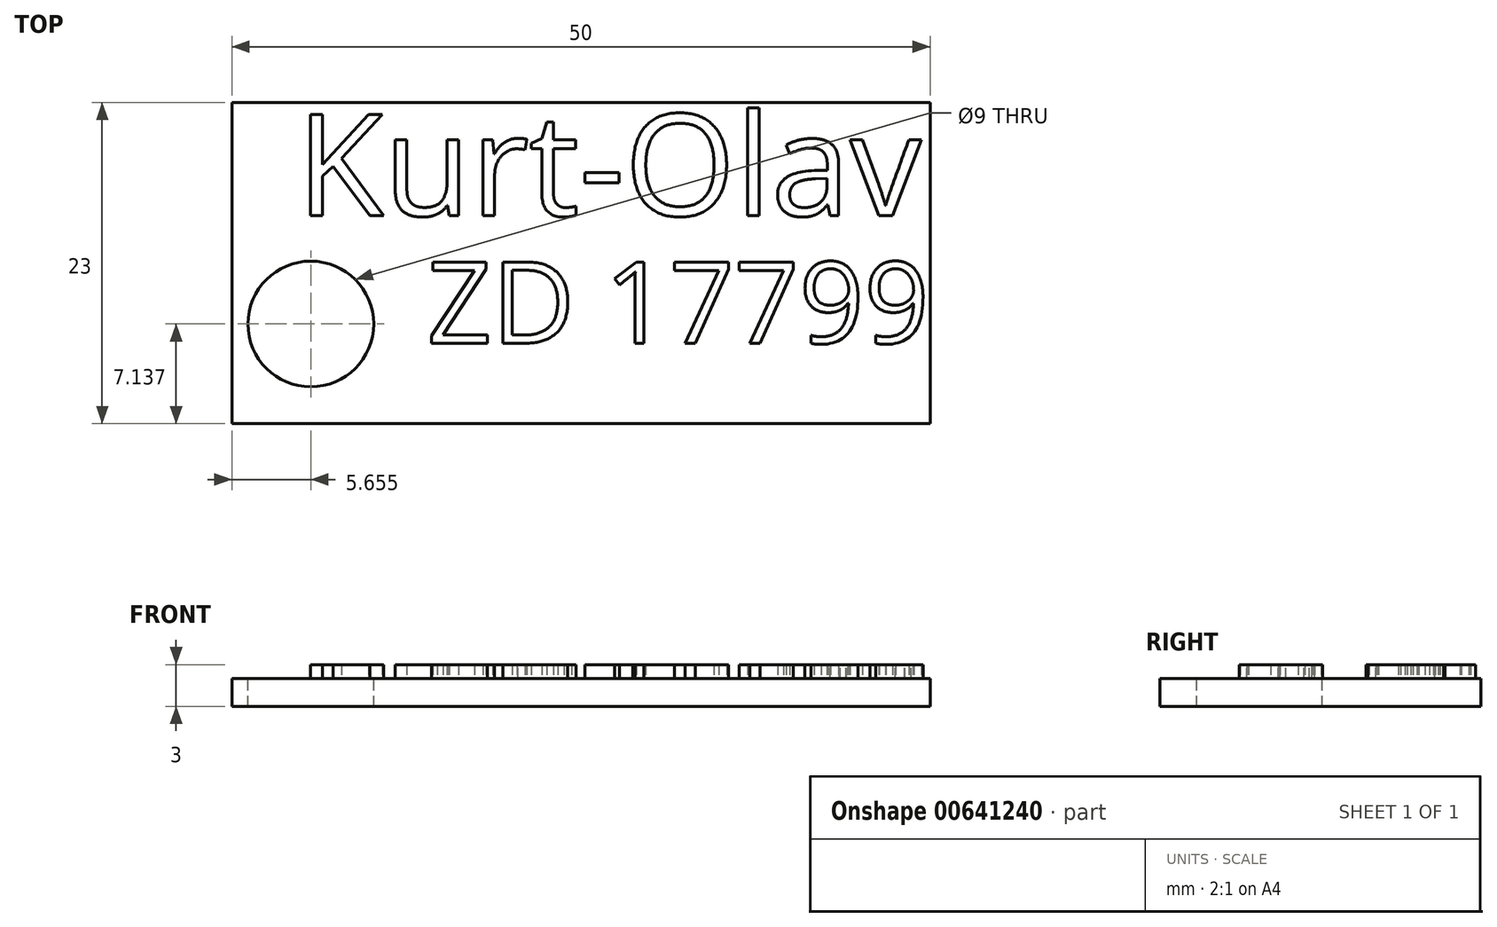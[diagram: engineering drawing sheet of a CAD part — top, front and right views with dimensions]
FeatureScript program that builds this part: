
annotation { "Feature Type Name" : "Feature", "Feature Type Description" : "" }
export const myFeature = defineFeature(function(context is Context, id is Id, definition is map)
    precondition{}
    {
        {
            var Q0;
            Q0=qCreatedBy(makeId("Top.planeOp"),FACE);
            var sketch = newSketch(context, id + "F0", { "sketchPlane" : qUnion([Q0])});
            skLineSegment(sketch, "E0.bottom", {"start": v(25, -11.5) * mm, "end": v(-25, -11.5) * mm});
            skLineSegment(sketch, "E0.top", {"start": v(25, 11.5) * mm, "end": v(-25, 11.5) * mm});
            skLineSegment(sketch, "E0.left", {"start": v(25, -11.5) * mm, "end": v(25, 11.5) * mm});
            skLineSegment(sketch, "E0.right", {"start": v(-25, -11.5) * mm, "end": v(-25, 11.5) * mm});
            skPoint(sketch, "E0.middle", {"position": v(0, 0) * mm});
            skSolve(sketch);
        }
        {
            var Q0;
            Q0=makeQuery(id+"F0.imprint","IMPRINT",FACE,{"disambiguationData":[TD([[makeQuery(id+"F0.imprint","IMPRINT",EDGE,{"derivedFrom":sQuery(id+"F0.wireOp",EDGE,"E0.bottom")}),-1.0]])]});
            extrude(context, id + "F1", {"entities" : qUnion([Q0]), "depth" : 2 * mm, "offsetDistance" : 25 * mm});
        }
        {
            var Q0;
            Q0=makeQuery(id+"F1.opExtrude","CAP_FACE",FACE,{"disambiguationData":[OSD([sQuery(id+"F0.wireOp",EDGE,"E0.bottom"),sQuery(id+"F0.wireOp",EDGE,"E0.top"),sQuery(id+"F0.wireOp",EDGE,"E0.left"),sQuery(id+"F0.wireOp",EDGE,"E0.right")])],"isStart":false});
            var sketch = newSketch(context, id + "F2", { "sketchPlane" : qUnion([Q0])});
            skText(sketch, "E1", { "text": "Kurt-Olav", "fontName": "OpenSans-Regular.ttf"});
            const initialGuessF2  = {"E1": [-0.02036, 0.00339, 1, 0, 0.00732]};
            skSetInitialGuess(sketch, initialGuessF2);
            skSolve(sketch);
        }
        {
            var Q0;
            Q0 = qSketchRegion(id + "F2", true);
            extrude(context, id + "F3", {"entities" : qUnion([Q0]), "operationType" : NewBodyOperationType.ADD, "depth" : 1 * mm, "offsetDistance" : 25 * mm});
        }
        {
            var Q0;
            {var subQ0=sQuery(id+"F0.wireOp",EDGE,"E0.top");var subQ1=sQuery(id+"F0.wireOp",EDGE,"E0.right");var subQ2=sQuery(id+"F0.wireOp",EDGE,"E0.bottom");var subQ3=sQuery(id+"F0.wireOp",EDGE,"E0.left");Q0=makeQuery(id+"F3.boolean.opBoolean","SPLIT",FACE,{"disambiguationData":[TD([makeQuery(id+"F1.opExtrude","SWEPT_FACE",FACE,{"disambiguationData":[OSD([subQ2])]})])],"derivedFrom":makeQuery(id+"F1.opExtrude","CAP_FACE",FACE,{"disambiguationData":[OSD([subQ2,subQ0,subQ3,subQ1])],"isStart":false})});}
            var sketch = newSketch(context, id + "F4", { "sketchPlane" : qUnion([Q0])});
            skText(sketch, "E2", { "text": "ZD 17799", "fontName": "OpenSans-Regular.ttf"});
            const initialGuessF4  = {"E2": [-0.01103, -0.00574, 1, 0, 0.00586]};
            skSetInitialGuess(sketch, initialGuessF4);
            skSolve(sketch);
        }
        {
            var Q0;
            Q0 = qSketchRegion(id + "F4", true);
            extrude(context, id + "F5", {"entities" : qUnion([Q0]), "operationType" : NewBodyOperationType.ADD, "depth" : 1 * mm, "offsetDistance" : 25 * mm});
        }
        {
            var Q0;
            {var subQ55=sQuery(id+"F0.wireOp",EDGE,"E0.top");var subQ59=sQuery(id+"F0.wireOp",EDGE,"E0.right");var subQ65=sQuery(id+"F0.wireOp",EDGE,"E0.bottom");var subQ66=makeQuery(id+"F1.opExtrude","SWEPT_FACE",FACE,{"disambiguationData":[OSD([subQ65])]});var subQ68=sQuery(id+"F0.wireOp",EDGE,"E0.left");Q0=makeQuery(id+"F5.boolean.opBoolean","SPLIT",FACE,{"disambiguationData":[TD([subQ66])],"derivedFrom":makeQuery(id+"F3.boolean.opBoolean","SPLIT",FACE,{"disambiguationData":[TD([subQ66])],"derivedFrom":makeQuery(id+"F1.opExtrude","CAP_FACE",FACE,{"disambiguationData":[OSD([subQ65,subQ55,subQ68,subQ59])],"isStart":false})})});}
            var sketch = newSketch(context, id + "F6", { "sketchPlane" : qUnion([Q0])});
            skPoint(sketch, "E3", {"position": v(-19.34, -4.36) * mm});
            skSolve(sketch);
        }
        {
            var Q0;
            Q0=sQuery(id+"F6.wireOp",VERTEX,"E3");
            var Q1;
            Q1=makeQuery(id+"F1.opExtrude","SWEPT_BODY",BODY,{"disambiguationData":[OSD([sQuery(id+"F0.wireOp",EDGE,"E0.bottom"),sQuery(id+"F0.wireOp",EDGE,"E0.top"),sQuery(id+"F0.wireOp",EDGE,"E0.left"),sQuery(id+"F0.wireOp",EDGE,"E0.right")])]});
            hole(context, id + "F7", {"style" : HoleStyle.C_BORE, "endStyle" : HoleEndStyle.THROUGH, "holeDiameter" : 3 * mm, "cBoreDiameter" : 9 * mm, "cBoreDepth" : 2 * mm, "majorDiameter" : 5 * mm, "isTappedThrough" : true, "tappedDepth" : 12 * mm, "tapClearance" : 3, "locations" : qUnion([Q0]), "scope" : qUnion([Q1])});
        }
    });
